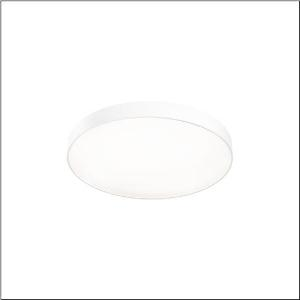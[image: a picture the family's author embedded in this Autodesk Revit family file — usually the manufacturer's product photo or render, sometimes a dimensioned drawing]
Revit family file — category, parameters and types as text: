
# Revit family: round_21_m_51mr36fm8421w
name_source: partatom
category: Lighting Fixtures
units: mm (PartAtom-declared; Revit-internal decimal feet)

## family parameters
Cut with Voids When Loaded = No
Host = Face
Light Source = No
Part Type = Normal
Room Calculation Point = No
Round Connector Dimension = Use Diameter
Shared = No

## types (1)
- --- (1 x LED, 8140 lm, 61.1 W, 4000K)
    Apparent Load = 61 VA
    CIE Flux Codes = 49 80 96 100 100
    Color Rendering = 80
    Color Temperature = 4000K
    Default Elevation = 1800 mm
    Description = Round 21 M, wall and ceiling luminaire, primary optical cover: cover, of PMMA, opal, light emission: direct distribution, primary light characteristic: symmetric, installation type: surface-mounted, suspended mounting, LED, rated luminous flux: 8.140lm, luminous efficacy: 133lm/W, light colour: 840, colour temperature: 4000K, with terminal, 3-pole, mains connection: 230V, AC, 50/60Hz, rated input power: 61W, housing, of aluminium, coated, white, diameter: 600mm, height: 62mm, protection rating (complete): IP40, insulation class (complete): insulation class I (protective earthing), certification: CE, impact resistance: IK04, permissible operating ambient temperature: -10..+35°C, packaging unit: 1 piece
    Height = 87 mm
    Lamp = 1 x LED
    Lamp Light Flux = 8140 lm
    Lamp Power = 61.1 W
    Lamp count = 1
    Length = 600 mm
    Luminous efficacy = 133 lm/W
    Manufacturer = Siteco
    ModVariant = No
    Model = 51MR36FM8421W
    Mounting Place = Ceiling
    Mounting Type = Surface mounted
    Number of Poles = 1
    OnlyDefault = Yes
    Power Factor = 1
    Product Name = Round 21 M
    Product group = wall and ceiling luminaire
    ProductGroupID = 301
    Protection Class = Protection class I
    Protection Degree = IP 40
    RLX_Detail_Level = 1
    RLX_Emergency_Light_Flux = 0 lm
    RLX_Emergency_Type = 0
    RLX_Emergency_Type_DB = No
    RlxData = <blob elided: 14289 chars, md5=bd30ca6b>
    Socket = socket
    Standby Power = 0 W
    System Light Flux = 8140 lm
    System Power = 61 W
    Type Comments = factory setting: luminous flux: 100 % | (ON | ON | ON | ON) | 700 mA
    Type Image = l_1258330.jpg
    URL = http://relux.com
    VarID = @adj_013401
    Voltage = 0 V
    Weight = 0.00 kg
    Width = 0 mm  [stored 0 ft]

note: [stored X ft] marks values corroborated as IEEE doubles in the binary element streams (Revit-internal decimal feet)

## geometry (parser evidence)
native form markers: Sweep x12
no freeform markers — native parametric forms only
